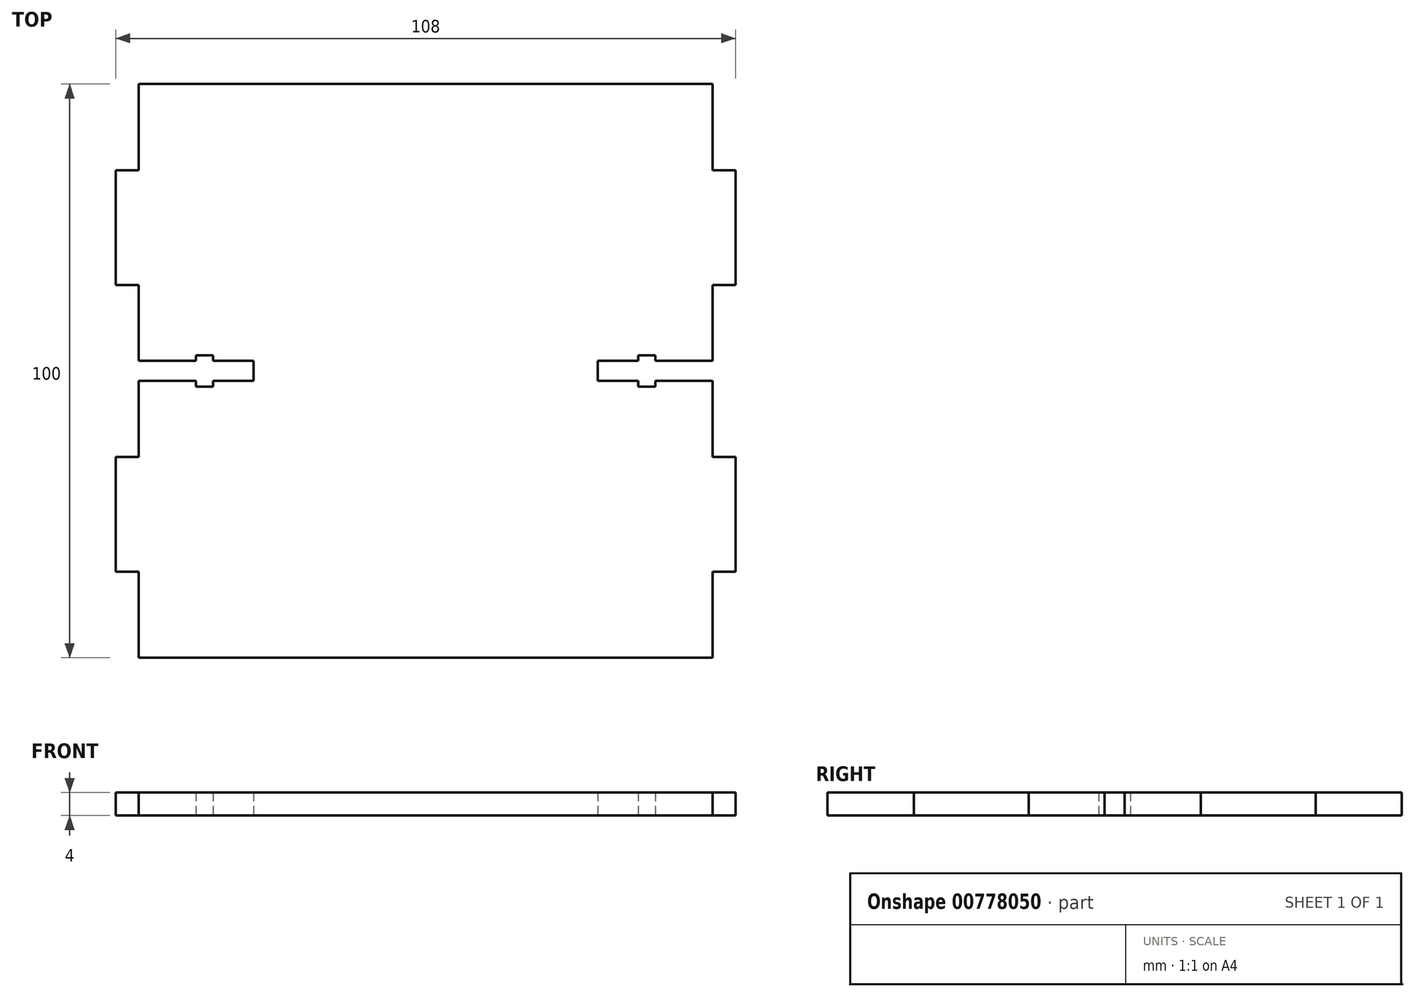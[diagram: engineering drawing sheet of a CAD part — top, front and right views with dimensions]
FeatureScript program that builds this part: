
annotation { "Feature Type Name" : "Feature", "Feature Type Description" : "" }
export const myFeature = defineFeature(function(context is Context, id is Id, definition is map)
    precondition{}
    {
        {
            var Q0;
            Q0=qCreatedBy(makeId("Top.planeOp"),FACE);
            var sketch = newSketch(context, id + "F0", { "sketchPlane" : qUnion([Q0])});
            skLineSegment(sketch, "E0.bottom", {"start": v(50, -50) * mm, "end": v(-50, -50) * mm});
            skLineSegment(sketch, "E0.top", {"start": v(50, 50) * mm, "end": v(-50, 50) * mm});
            skLineSegment(sketch, "E0.left", {"start": v(50, -50) * mm, "end": v(50, -35) * mm});
            skLineSegment(sketch, "E0.right", {"start": v(-50, -50) * mm, "end": v(-50, -35) * mm});
            skPoint(sketch, "E0.middle", {"position": v(0, 0) * mm});
            skLineSegment(sketch, "E1", {"start": v(-54, 35) * mm, "end": v(-50, 35) * mm});
            skLineSegment(sketch, "E2", {"start": v(54, 35) * mm, "end": v(54, 15) * mm});
            skLineSegment(sketch, "E3", {"start": v(54, 15) * mm, "end": v(50, 15) * mm});
            skLineSegment(sketch, "E4", {"start": v(-54, 15) * mm, "end": v(-54, 35) * mm});
            skLineSegment(sketch, "E5", {"start": v(-54, -15) * mm, "end": v(-50, -15) * mm});
            skLineSegment(sketch, "E6", {"start": v(54, -15) * mm, "end": v(54, -35) * mm});
            skLineSegment(sketch, "E7", {"start": v(54, -35) * mm, "end": v(50, -35) * mm});
            skLineSegment(sketch, "E8", {"start": v(-54, -35) * mm, "end": v(-54, -15) * mm});
            skLineSegment(sketch, "E9.trimOffspring", {"start": v(-50, 35) * mm, "end": v(-50, 50) * mm});
            skLineSegment(sketch, "E10.trimOffspring", {"start": v(-50, -15) * mm, "end": v(-50, -1.75) * mm});
            skLineSegment(sketch, "E11.trimOffspring", {"start": v(50, -15) * mm, "end": v(50, -1.75) * mm});
            skLineSegment(sketch, "E12.trimOffspring", {"start": v(50, 35) * mm, "end": v(50, 50) * mm});
            skLineSegment(sketch, "E13.trimOffspring", {"start": v(50, 35) * mm, "end": v(54, 35) * mm});
            skLineSegment(sketch, "E14.trimOffspring", {"start": v(-50, 15) * mm, "end": v(-54, 15) * mm});
            skLineSegment(sketch, "E15.trimOffspring", {"start": v(50, -15) * mm, "end": v(54, -15) * mm});
            skLineSegment(sketch, "E16.trimOffspring", {"start": v(-50, -35) * mm, "end": v(-54, -35) * mm});
            skLineSegment(sketch, "E17", {"start": v(-50, 1.75) * mm, "end": v(-40, 1.75) * mm});
            skLineSegment(sketch, "E18.0", {"start": v(-50, -1.75) * mm, "end": v(-40, -1.75) * mm});
            skLineSegment(sketch, "E19.0", {"start": v(-40, 2.75) * mm, "end": v(-37, 2.75) * mm});
            skLineSegment(sketch, "E20.0", {"start": v(-40, -2.75) * mm, "end": v(-37, -2.75) * mm});
            skLineSegment(sketch, "E21", {"start": v(-40, 2.75) * mm, "end": v(-40, 1.75) * mm});
            skLineSegment(sketch, "E22", {"start": v(-37, 2.75) * mm, "end": v(-37, 1.75) * mm});
            skLineSegment(sketch, "E23", {"start": v(-30, 1.75) * mm, "end": v(-30, -1.75) * mm});
            skLineSegment(sketch, "E24.trimOffspring", {"start": v(-40, -1.75) * mm, "end": v(-40, -2.75) * mm});
            skLineSegment(sketch, "E25.trimOffspring", {"start": v(-37, -1.75) * mm, "end": v(-37, -2.75) * mm});
            skLineSegment(sketch, "E26.trimOffspring", {"start": v(-37, 1.75) * mm, "end": v(-30, 1.75) * mm});
            skLineSegment(sketch, "E27.trimOffspring", {"start": v(-37, -1.75) * mm, "end": v(-30, -1.75) * mm});
            skLineSegment(sketch, "E28", {"start": v(40, 2.75) * mm, "end": v(40, 1.75) * mm});
            skLineSegment(sketch, "E29", {"start": v(37, 2.75) * mm, "end": v(37, 1.75) * mm});
            skLineSegment(sketch, "E30", {"start": v(30, 1.75) * mm, "end": v(30, -1.75) * mm});
            skLineSegment(sketch, "E31.trimOffspring", {"start": v(40, -1.75) * mm, "end": v(40, -2.75) * mm});
            skLineSegment(sketch, "E32.trimOffspring", {"start": v(37, -1.75) * mm, "end": v(37, -2.75) * mm});
            skLineSegment(sketch, "E33.trimOffspring", {"start": v(40, 1.75) * mm, "end": v(50, 1.75) * mm});
            skLineSegment(sketch, "E34.trimOffspring", {"start": v(40, -1.75) * mm, "end": v(50, -1.75) * mm});
            skLineSegment(sketch, "E35.trimOffspring", {"start": v(37, -2.75) * mm, "end": v(40, -2.75) * mm});
            skLineSegment(sketch, "E36.trimOffspring", {"start": v(37, 2.75) * mm, "end": v(40, 2.75) * mm});
            skLineSegment(sketch, "E37.trimOffspring", {"start": v(30, 1.75) * mm, "end": v(37, 1.75) * mm});
            skLineSegment(sketch, "E38.trimOffspring", {"start": v(30, -1.75) * mm, "end": v(37, -1.75) * mm});
            skLineSegment(sketch, "E39.trimOffspring", {"start": v(-50, 1.75) * mm, "end": v(-50, 15) * mm});
            skLineSegment(sketch, "E40.trimOffspring", {"start": v(50, 1.75) * mm, "end": v(50, 15) * mm});
            skSolve(sketch);
        }
        {
            var Q0;
            Q0=makeQuery(id+"F0.imprint","IMPRINT",FACE,{"disambiguationData":[TD([[makeQuery(id+"F0.imprint","IMPRINT",EDGE,{"derivedFrom":sQuery(id+"F0.wireOp",EDGE,"E0.bottom")}),-1.0]])]});
            extrude(context, id + "F1", {"entities" : qUnion([Q0]), "depth" : (4) * mm, "offsetDistance" : 25 * mm});
        }
    });
